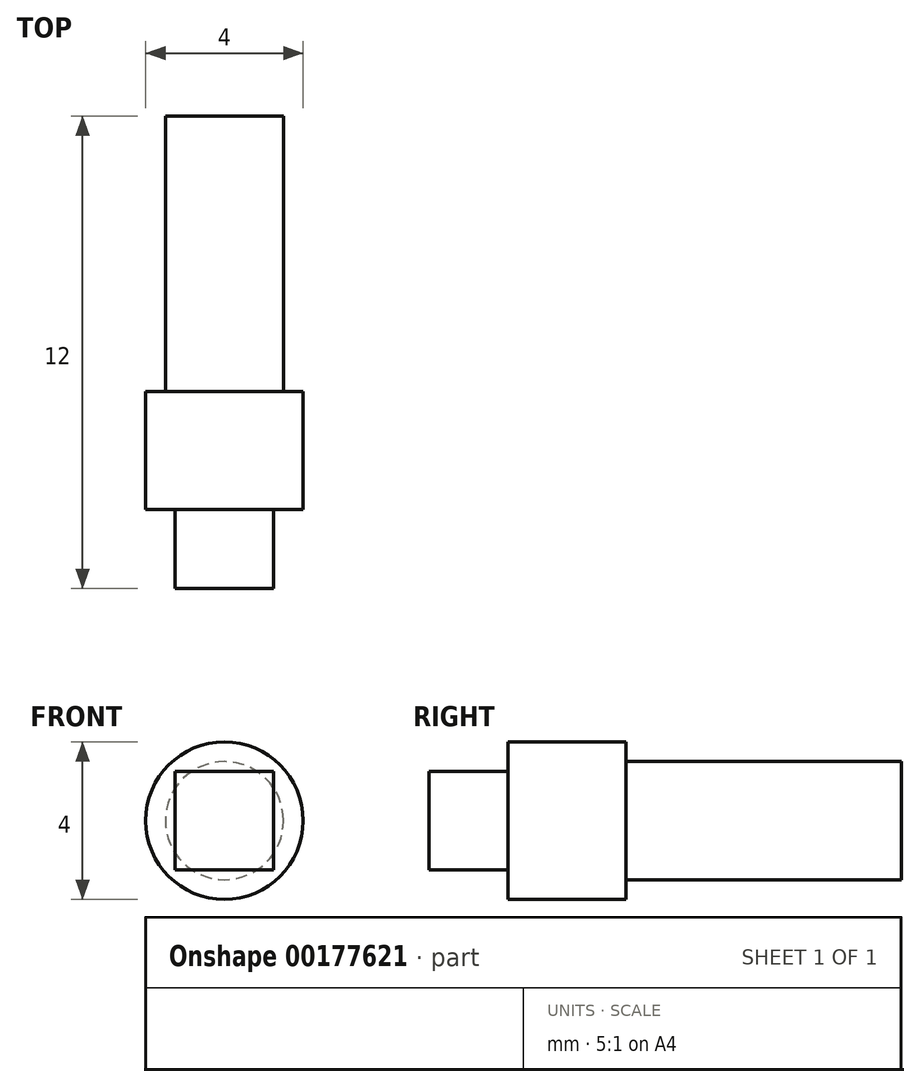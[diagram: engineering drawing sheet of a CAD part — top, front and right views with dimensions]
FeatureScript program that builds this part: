
annotation { "Feature Type Name" : "Feature", "Feature Type Description" : "" }
export const myFeature = defineFeature(function(context is Context, id is Id, definition is map)
    precondition{}
    {
        {
            var Q0;
            Q0=qCreatedBy(makeId("Front.planeOp"),FACE);
            var sketch = newSketch(context, id + "F0", { "sketchPlane" : qUnion([Q0])});
            skCircle(sketch, "E0", {"center": v(0, 0) * mm, "radius": 1.5 * mm});
            skSolve(sketch);
        }
        {
            var Q0;
            Q0=qSketchRegion(id+"F0",true);
            extrude(context, id + "F1", {"entities" : qUnion([Q0]), "depth" : 7 * mm});
        }
        {
            var Q0;
            Q0=makeQuery(id+"F1.opExtrude","CAP_FACE",FACE,{"disambiguationData":[OSD([sQuery(id+"F0.wireOp",EDGE,"E0")])],"isStart":false});
            var sketch = newSketch(context, id + "F2", { "sketchPlane" : qUnion([Q0])});
            skCircle(sketch, "E1", {"center": v(0, 0) * mm, "radius": 2 * mm});
            skSolve(sketch);
        }
        {
            var Q0;
            Q0=qSketchRegion(id+"F2",true);
            extrude(context, id + "F3", {"entities" : qUnion([Q0]), "operationType" : NewBodyOperationType.ADD, "depth" : 3 * mm});
        }
        {
            var Q0;
            Q0=makeQuery(id+"F3.opExtrude","CAP_FACE",FACE,{"disambiguationData":[OSD([sQuery(id+"F2.wireOp",EDGE,"E1")])],"isStart":false});
            var sketch = newSketch(context, id + "F4", { "sketchPlane" : qUnion([Q0])});
            skLineSegment(sketch, "E2.bottom", {"start": v(1.25, 1.25) * mm, "end": v(-1.25, 1.25) * mm});
            skLineSegment(sketch, "E2.top", {"start": v(1.25, -1.25) * mm, "end": v(-1.25, -1.25) * mm});
            skLineSegment(sketch, "E2.left", {"start": v(1.25, 1.25) * mm, "end": v(1.25, -1.25) * mm});
            skLineSegment(sketch, "E2.right", {"start": v(-1.25, 1.25) * mm, "end": v(-1.25, -1.25) * mm});
            skPoint(sketch, "E2.middle", {"position": v(0, 0) * mm});
            skSolve(sketch);
        }
        {
            var Q0;
            Q0=qSketchRegion(id+"F4",true);
            extrude(context, id + "F5", {"entities" : qUnion([Q0]), "operationType" : NewBodyOperationType.ADD, "depth" : 2 * mm});
        }
    });
